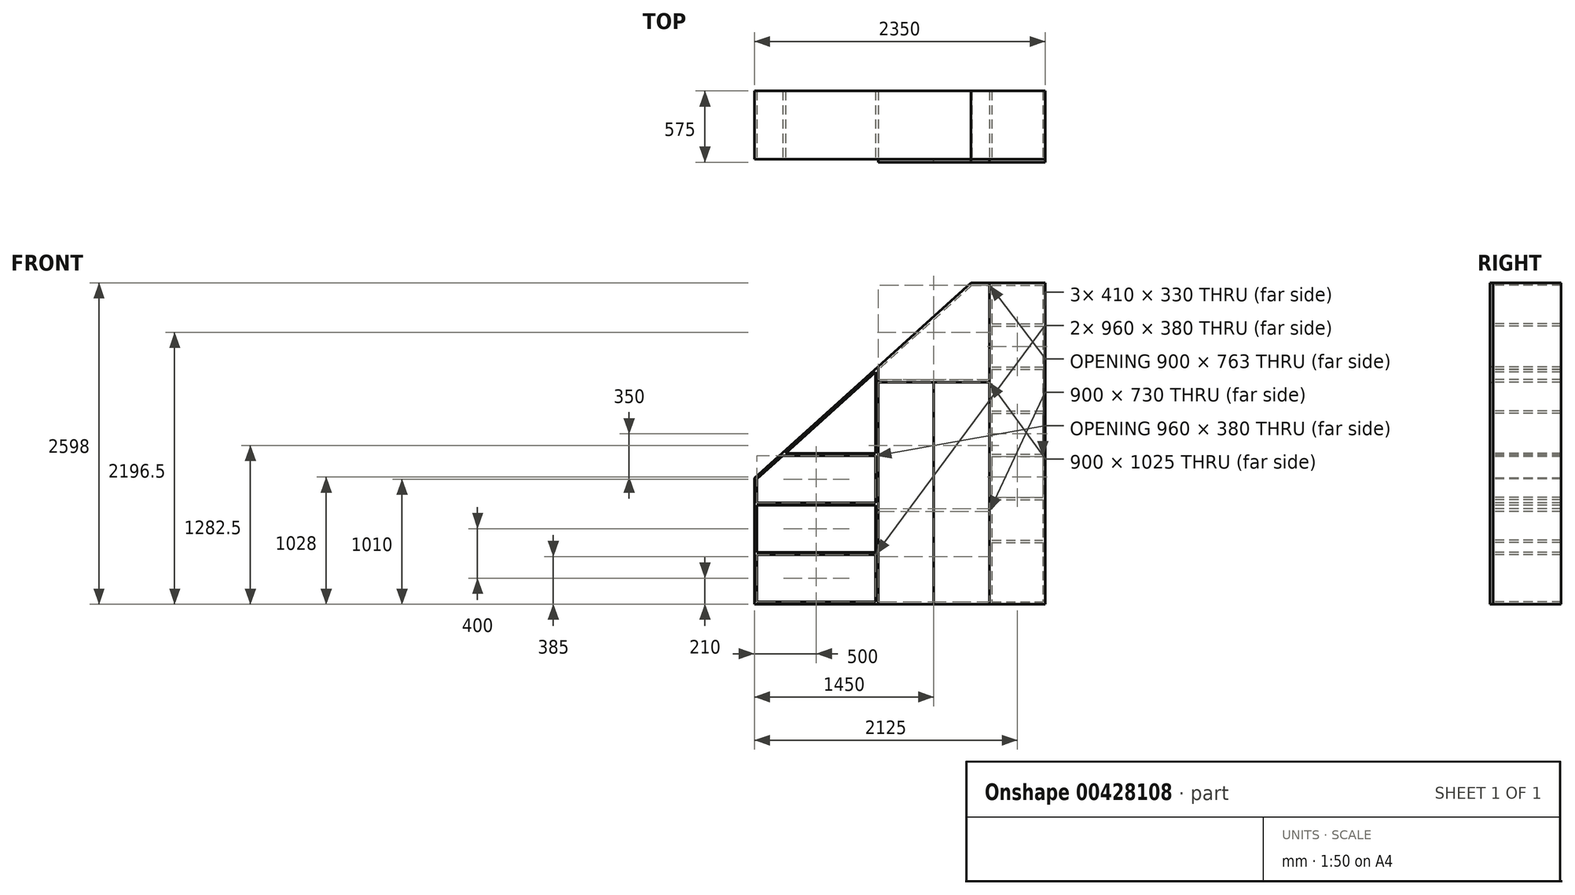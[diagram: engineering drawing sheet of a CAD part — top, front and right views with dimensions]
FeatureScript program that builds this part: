
annotation { "Feature Type Name" : "Feature", "Feature Type Description" : "" }
export const myFeature = defineFeature(function(context is Context, id is Id, definition is map)
    precondition{}
    {
        {
            var Q0;
            Q0=qCreatedBy(makeId("Front.planeOp"),FACE);
            var sketch = newSketch(context, id + "F0", { "sketchPlane" : qUnion([Q0])});
            skLineSegment(sketch, "E0.bottom", {"start": v(500, 1299) * mm, "end": v(1100, 1299) * mm});
            skLineSegment(sketch, "E0.top", {"start": v(-1250, -1299) * mm, "end": v(-250, -1299) * mm});
            skLineSegment(sketch, "E0.right", {"start": v(1100, 1299) * mm, "end": v(1100, -436) * mm});
            skPoint(sketch, "E0.middle", {"position": v(0, 0) * mm});
            skLineSegment(sketch, "E1.0", {"start": v(650, 1279) * mm, "end": v(650, 516) * mm});
            skLineSegment(sketch, "E2.0", {"start": v(200, 1028.49) * mm, "end": v(200, 516) * mm});
            skLineSegment(sketch, "E3.0", {"start": v(-250, 595.78) * mm, "end": v(-250, 516) * mm});
            skLineSegment(sketch, "E4.trimOffspring", {"start": v(650, -1299) * mm, "end": v(1100, -1299) * mm});
            skLineSegment(sketch, "E5", {"start": v(-250, -1299) * mm, "end": v(200, -1299) * mm});
            skLineSegment(sketch, "E6", {"start": v(650, -1299) * mm, "end": v(200, -1299) * mm});
            skLineSegment(sketch, "E7.0", {"start": v(650, -1049) * mm, "end": v(200, -1049) * mm});
            skLineSegment(sketch, "E7.1", {"start": v(-250, -1049) * mm, "end": v(200, -1049) * mm});
            skLineSegment(sketch, "E8.0", {"start": v(650, -799) * mm, "end": v(200, -799) * mm});
            skLineSegment(sketch, "E8.1", {"start": v(-250, -799) * mm, "end": v(200, -799) * mm});
            skLineSegment(sketch, "E9.0", {"start": v(650, -549) * mm, "end": v(200, -549) * mm});
            skLineSegment(sketch, "E9.1", {"start": v(-250, -549) * mm, "end": v(200, -549) * mm});
            skLineSegment(sketch, "E10.0", {"start": v(-250, 516) * mm, "end": v(200, 516) * mm});
            skLineSegment(sketch, "E11", {"start": v(200, 516) * mm, "end": v(650, 516) * mm});
            skLineSegment(sketch, "E12.0", {"start": v(670, 949) * mm, "end": v(1080, 949) * mm});
            skLineSegment(sketch, "E13.0", {"start": v(670, 599) * mm, "end": v(1080, 599) * mm});
            skLineSegment(sketch, "E14.0", {"start": v(670, 264) * mm, "end": v(1080, 264) * mm});
            skLineSegment(sketch, "E15.0", {"start": v(670, -86) * mm, "end": v(1080, -86) * mm});
            skLineSegment(sketch, "E16.0", {"start": v(670, -436) * mm, "end": v(1080, -436) * mm});
            skLineSegment(sketch, "E17.0", {"start": v(670, -801) * mm, "end": v(1080, -801) * mm});
            skLineSegment(sketch, "E18.0", {"start": v(-1230, -899) * mm, "end": v(-270, -899) * mm});
            skLineSegment(sketch, "E19.0", {"start": v(-1230, -499) * mm, "end": v(-270, -499) * mm});
            skLineSegment(sketch, "E20.0", {"start": v(-1020.51, -99) * mm, "end": v(-270, -99) * mm});
            skLineSegment(sketch, "E21.0", {"start": v(-1250, -279) * mm, "end": v(-1250, -1299) * mm});
            skLineSegment(sketch, "E22", {"start": v(500, 1299) * mm, "end": v(-1250, -279) * mm});
            skLineSegment(sketch, "E23", {"start": v(-250, 441.27) * mm, "end": v(650, 441.27) * mm});
            skLineSegment(sketch, "E24.0", {"start": v(-250, 431.27) * mm, "end": v(650, 431.27) * mm});
            skLineSegment(sketch, "E25", {"start": v(200, 516) * mm, "end": v(200, -1279) * mm});
            skLineSegment(sketch, "E26.0", {"start": v(-1230, -287.9) * mm, "end": v(-1230, -479) * mm});
            skLineSegment(sketch, "E27.0", {"start": v(-1230, -1279) * mm, "end": v(-270, -1279) * mm});
            skLineSegment(sketch, "E28.0", {"start": v(-1230, -879) * mm, "end": v(-270, -879) * mm});
            skLineSegment(sketch, "E29.0", {"start": v(-1250, -479) * mm, "end": v(-1247.8, -479) * mm});
            skLineSegment(sketch, "E30.0", {"start": v(507.69, 1279) * mm, "end": v(-250, 595.78) * mm});
            skLineSegment(sketch, "E31.0", {"start": v(507.69, 1279) * mm, "end": v(1080, 1279) * mm});
            skLineSegment(sketch, "E32.0", {"start": v(670, 969) * mm, "end": v(1080, 969) * mm});
            skLineSegment(sketch, "E33.0", {"start": v(670, 619) * mm, "end": v(1080, 619) * mm});
            skLineSegment(sketch, "E34.0", {"start": v(670, 244) * mm, "end": v(1080, 244) * mm});
            skLineSegment(sketch, "E35.0", {"start": v(670, -106) * mm, "end": v(1080, -106) * mm});
            skLineSegment(sketch, "E36.0", {"start": v(670, -456) * mm, "end": v(1080, -456) * mm});
            skLineSegment(sketch, "E37.0", {"start": v(670, -781) * mm, "end": v(1080, -781) * mm});
            skLineSegment(sketch, "E38.0", {"start": v(-250, -1279) * mm, "end": v(200, -1279) * mm});
            skLineSegment(sketch, "E38.1", {"start": v(650, -1279) * mm, "end": v(200, -1279) * mm});
            skLineSegment(sketch, "E39.0", {"start": v(670, -1279) * mm, "end": v(1080, -1279) * mm});
            skLineSegment(sketch, "E40.0", {"start": v(1080, 1279) * mm, "end": v(1080, 969) * mm});
            skLineSegment(sketch, "E41.0", {"start": v(670, 1279) * mm, "end": v(670, 969) * mm});
            skLineSegment(sketch, "E42.0", {"start": v(-270, 577.75) * mm, "end": v(-270, -79) * mm});
            skPoint(sketch, "E43.orphan", {"position": v(-1250, -899) * mm});
            skLineSegment(sketch, "E44.trimOffspring", {"start": v(-1230, -899) * mm, "end": v(-1230, -1279) * mm});
            skLineSegment(sketch, "E45.trimOffspring", {"start": v(-270, -899) * mm, "end": v(-270, -1279) * mm});
            skLineSegment(sketch, "E46.trimOffspring", {"start": v(-250, -899) * mm, "end": v(-250, -1279) * mm});
            skLineSegment(sketch, "E47.trimOffspring", {"start": v(-1230, -479) * mm, "end": v(-270, -479) * mm});
            skLineSegment(sketch, "E48.trimOffspring", {"start": v(-1247.8, -479) * mm, "end": v(-1250, -480.98) * mm});
            skLineSegment(sketch, "E49.trimOffspring", {"start": v(-1230, -499) * mm, "end": v(-1230, -879) * mm});
            skLineSegment(sketch, "E50.trimOffspring", {"start": v(-998.33, -79) * mm, "end": v(-270, -79) * mm});
            skLineSegment(sketch, "E51.trimOffspring", {"start": v(-1020.51, -99) * mm, "end": v(-1230, -287.9) * mm});
            skLineSegment(sketch, "E52.trimOffspring", {"start": v(-270, -99) * mm, "end": v(-270, -479) * mm});
            skLineSegment(sketch, "E53", {"start": v(-250, -879) * mm, "end": v(-250, -899) * mm});
            skPoint(sketch, "E54.orphan", {"position": v(1100, -801) * mm});
            skLineSegment(sketch, "E55.trimOffspring", {"start": v(1080, -801) * mm, "end": v(1080, -1279) * mm});
            skLineSegment(sketch, "E56.trimOffspring", {"start": v(670, -801) * mm, "end": v(670, -1279) * mm});
            skLineSegment(sketch, "E57.trimOffspring", {"start": v(670, -456) * mm, "end": v(670, -781) * mm});
            skLineSegment(sketch, "E58.trimOffspring", {"start": v(1080, -456) * mm, "end": v(1080, -781) * mm});
            skLineSegment(sketch, "E59.trimOffspring", {"start": v(1100, -456) * mm, "end": v(1100, -1299) * mm});
            skLineSegment(sketch, "E60", {"start": v(1100, -436) * mm, "end": v(1100, -456) * mm});
            skLineSegment(sketch, "E61.trimOffspring", {"start": v(1080, -106) * mm, "end": v(1080, -436) * mm});
            skLineSegment(sketch, "E62.trimOffspring", {"start": v(670, -106) * mm, "end": v(670, -436) * mm});
            skLineSegment(sketch, "E63.trimOffspring", {"start": v(670, 244) * mm, "end": v(670, -86) * mm});
            skLineSegment(sketch, "E64.trimOffspring", {"start": v(1080, 244) * mm, "end": v(1080, -86) * mm});
            skLineSegment(sketch, "E65.trimOffspring", {"start": v(1080, 599) * mm, "end": v(1080, 264) * mm});
            skLineSegment(sketch, "E66.trimOffspring", {"start": v(670, 599) * mm, "end": v(670, 264) * mm});
            skLineSegment(sketch, "E67.trimOffspring", {"start": v(670, 949) * mm, "end": v(670, 619) * mm});
            skLineSegment(sketch, "E68.trimOffspring", {"start": v(1080, 949) * mm, "end": v(1080, 619) * mm});
            skLineSegment(sketch, "E69.trimOffspring", {"start": v(-270, 577.75) * mm, "end": v(-998.33, -79) * mm});
            skLineSegment(sketch, "E70.0", {"start": v(650, -529) * mm, "end": v(200, -529) * mm});
            skLineSegment(sketch, "E70.1", {"start": v(-250, -529) * mm, "end": v(200, -529) * mm});
            skLineSegment(sketch, "E71.0", {"start": v(200, 496) * mm, "end": v(650, 496) * mm});
            skLineSegment(sketch, "E71.1", {"start": v(-250, 496) * mm, "end": v(200, 496) * mm});
            skLineSegment(sketch, "E72.trimOffspring", {"start": v(-270, -499) * mm, "end": v(-270, -879) * mm});
            skLineSegment(sketch, "E73.trimOffspring", {"start": v(-250, -549) * mm, "end": v(-250, -879) * mm});
            skLineSegment(sketch, "E74.trimOffspring", {"start": v(650, -549) * mm, "end": v(650, -1279) * mm});
            skLineSegment(sketch, "E75.trimOffspring", {"start": v(-250, 496) * mm, "end": v(-250, -529) * mm});
            skLineSegment(sketch, "E76.trimOffspring", {"start": v(650, 496) * mm, "end": v(650, -529) * mm});
            skLineSegment(sketch, "E77", {"start": v(-270, 577.75) * mm, "end": v(-250, 595.78) * mm});
            skLineSegment(sketch, "E78", {"start": v(-998.33, -79) * mm, "end": v(-1020.51, -99) * mm});
            skLineSegment(sketch, "E79", {"start": v(-250, -529) * mm, "end": v(-250, -549) * mm});
            skLineSegment(sketch, "E80", {"start": v(-250, -1279) * mm, "end": v(-250, -1299) * mm});
            skLineSegment(sketch, "E81", {"start": v(200, -1279) * mm, "end": v(200, -1299) * mm});
            skLineSegment(sketch, "E82", {"start": v(650, -1279) * mm, "end": v(650, -1299) * mm});
            skLineSegment(sketch, "E83", {"start": v(650, -529) * mm, "end": v(650, -549) * mm});
            skLineSegment(sketch, "E84", {"start": v(-1230, -462.94) * mm, "end": v(-1247.8, -479) * mm});
            skLineSegment(sketch, "E85", {"start": v(650, 516) * mm, "end": v(650, 496) * mm});
            skLineSegment(sketch, "E86", {"start": v(650, 1279) * mm, "end": v(650, 1299) * mm});
            skLineSegment(sketch, "E87", {"start": v(-250, 516) * mm, "end": v(-250, 496) * mm});
            skLineSegment(sketch, "E88", {"start": v(-250, 595.78) * mm, "end": v(-250, 622.71) * mm});
            skSolve(sketch);
        }
        {
            var Q0;
            Q0 = qSketchRegion(id + "F0", true);
            var Q1;
            {var subQ1=sQuery(id+"F0.wireOp",EDGE,"E10.0");var subQ3=sQuery(id+"F0.wireOp",EDGE,"bf8423d4-a588-4095-a5d6-ed5b53389bde.0");var subQ4=makeQuery(id+"F0.imprint","INTERSECT",VERTEX,{"derivedFrom":[subQ1,subQ3]});Q1=makeQuery(id+"F0.imprint","IMPRINT",FACE,{"disambiguationData":[TD([[makeQuery(id+"F0.imprint","IMPRINT",EDGE,{"disambiguationData":[TD([[subQ4,-1.0]])],"derivedFrom":subQ3}),1.0]])]});}
            var Q2;
            {var subQ9=sQuery(id+"F0.wireOp",EDGE,"E3.0");Q2=makeQuery(id+"F0.imprint","IMPRINT",FACE,{"disambiguationData":[TD([[makeQuery(id+"F0.imprint","IMPRINT",EDGE,{"derivedFrom":subQ9}),-1.0]])]});}
            var Q3;
            {var subQ0=sQuery(id+"F0.wireOp",EDGE,"E78");Q3=makeQuery(id+"F0.imprint","IMPRINT",FACE,{"disambiguationData":[TD([[makeQuery(id+"F0.imprint","IMPRINT",EDGE,{"derivedFrom":subQ0}),1.0]])]});}
            var Q4;
            {var subQ0=sQuery(id+"F0.wireOp",EDGE,"E31.0");var subQ1=sQuery(id+"F0.wireOp",EDGE,"E1.0");var subQ2=makeQuery(id+"F0.imprint","INTERSECT",VERTEX,{"derivedFrom":[subQ1,subQ0]});Q4=makeQuery(id+"F0.imprint","IMPRINT",FACE,{"disambiguationData":[TD([[makeQuery(id+"F0.imprint","IMPRINT",EDGE,{"disambiguationData":[TD([[subQ2,-1.0]])],"derivedFrom":subQ1}),1.0]])]});}
            var Q5;
            {var subQ0=sQuery(id+"F0.wireOp",EDGE,"E9.1");Q5=makeQuery(id+"F0.imprint","IMPRINT",FACE,{"disambiguationData":[TD([[makeQuery(id+"F0.imprint","IMPRINT",EDGE,{"derivedFrom":subQ0}),1.0]])]});}
            var Q6;
            {var subQ0=sQuery(id+"F0.wireOp",EDGE,"E9.0");Q6=makeQuery(id+"F0.imprint","IMPRINT",FACE,{"disambiguationData":[TD([[makeQuery(id+"F0.imprint","IMPRINT",EDGE,{"derivedFrom":subQ0}),-1.0]])]});}
            var Q7;
            {var subQ0=sQuery(id+"F0.wireOp",EDGE,"E11");Q7=makeQuery(id+"F0.imprint","IMPRINT",FACE,{"disambiguationData":[TD([[makeQuery(id+"F0.imprint","IMPRINT",EDGE,{"derivedFrom":subQ0}),-1.0]])]});}
            var Q8;
            {var subQ0=sQuery(id+"F0.wireOp",EDGE,"E10.0");Q8=makeQuery(id+"F0.imprint","IMPRINT",FACE,{"disambiguationData":[TD([[makeQuery(id+"F0.imprint","IMPRINT",EDGE,{"derivedFrom":subQ0}),-1.0]])]});}
            extrude(context, id + "F1", {"entities" : qUnion([Q0, Q1, Q2, Q3, Q4, Q5, Q6, Q7, Q8]), "oppositeDirection" : true, "depth" : 550 * mm});
        }
        {
            var Q0;
            {var subQ1=sQuery(id+"F0.wireOp",EDGE,"E3.0");Q0=makeQuery(id+"F0.imprint","IMPRINT",FACE,{"disambiguationData":[TD([[makeQuery(id+"F0.imprint","IMPRINT",EDGE,{"derivedFrom":subQ1}),1.0]])]});}
            var Q1;
            {var subQ0=sQuery(id+"F0.wireOp",EDGE,"E10.0");Q1=makeQuery(id+"F0.imprint","IMPRINT",FACE,{"disambiguationData":[TD([[makeQuery(id+"F0.imprint","IMPRINT",EDGE,{"derivedFrom":subQ0}),-1.0]])]});}
            var Q2;
            {var subQ6=sQuery(id+"F0.wireOp",EDGE,"E1.0");Q2=makeQuery(id+"F0.imprint","IMPRINT",FACE,{"disambiguationData":[TD([[makeQuery(id+"F0.imprint","IMPRINT",EDGE,{"derivedFrom":subQ6}),-1.0]])]});}
            var Q3;
            {var subQ0=sQuery(id+"F0.wireOp",EDGE,"E11");Q3=makeQuery(id+"F0.imprint","IMPRINT",FACE,{"disambiguationData":[TD([[makeQuery(id+"F0.imprint","IMPRINT",EDGE,{"derivedFrom":subQ0}),-1.0]])]});}
            var Q4;
            {var subQ5=sQuery(id+"F0.wireOp",EDGE,"E88");Q4=makeQuery(id+"F0.imprint","IMPRINT",FACE,{"disambiguationData":[TD([[makeQuery(id+"F0.imprint","IMPRINT",EDGE,{"derivedFrom":subQ5}),-1.0]])]});}
            var Q5;
            {var subQ9=sQuery(id+"F0.wireOp",EDGE,"E86");Q5=makeQuery(id+"F0.imprint","IMPRINT",FACE,{"disambiguationData":[TD([[makeQuery(id+"F0.imprint","IMPRINT",EDGE,{"derivedFrom":subQ9}),1.0]])]});}
            extrude(context, id + "F2", {"entities" : qUnion([Q0, Q1, Q2, Q3, Q4, Q5]), "depth" : 25 * mm});
        }
        {
            var Q0;
            {var subQ5=sQuery(id+"F0.wireOp",EDGE,"E71.1");Q0=makeQuery(id+"F0.imprint","IMPRINT",FACE,{"disambiguationData":[TD([[makeQuery(id+"F0.imprint","IMPRINT",EDGE,{"derivedFrom":subQ5}),-1.0]])]});}
            var Q1;
            {var subQ5=sQuery(id+"F0.wireOp",EDGE,"E70.1");Q1=makeQuery(id+"F0.imprint","IMPRINT",FACE,{"disambiguationData":[TD([[makeQuery(id+"F0.imprint","IMPRINT",EDGE,{"derivedFrom":subQ5}),1.0]])]});}
            var Q2;
            {var subQ0=sQuery(id+"F0.wireOp",EDGE,"E75.trimOffspring");var subQ1=sQuery(id+"F0.wireOp",EDGE,"E23");var subQ2=makeQuery(id+"F0.imprint","INTERSECT",VERTEX,{"derivedFrom":[subQ1,subQ0]});Q2=makeQuery(id+"F0.imprint","IMPRINT",FACE,{"disambiguationData":[TD([[makeQuery(id+"F0.imprint","IMPRINT",EDGE,{"disambiguationData":[TD([[subQ2,-1.0]])],"derivedFrom":subQ1}),-1.0]])]});}
            var Q3;
            {var subQ0=sQuery(id+"F0.wireOp",EDGE,"E8.1");Q3=makeQuery(id+"F0.imprint","IMPRINT",FACE,{"disambiguationData":[TD([[makeQuery(id+"F0.imprint","IMPRINT",EDGE,{"derivedFrom":subQ0}),1.0]])]});}
            var Q4;
            {var subQ1=sQuery(id+"F0.wireOp",EDGE,"E7.1");Q4=makeQuery(id+"F0.imprint","IMPRINT",FACE,{"disambiguationData":[TD([[makeQuery(id+"F0.imprint","IMPRINT",EDGE,{"derivedFrom":subQ1}),1.0]])]});}
            var Q5;
            {var subQ0=sQuery(id+"F0.wireOp",EDGE,"E7.1");Q5=makeQuery(id+"F0.imprint","IMPRINT",FACE,{"disambiguationData":[TD([[makeQuery(id+"F0.imprint","IMPRINT",EDGE,{"derivedFrom":subQ0}),-1.0]])]});}
            var Q6;
            {var subQ0=sQuery(id+"F0.wireOp",EDGE,"E9.1");Q6=makeQuery(id+"F0.imprint","IMPRINT",FACE,{"disambiguationData":[TD([[makeQuery(id+"F0.imprint","IMPRINT",EDGE,{"derivedFrom":subQ0}),1.0]])]});}
            var Q7;
            Q7=makeQuery(id+"F0.imprint","IMPRINT",FACE,{"disambiguationData":[TD([[makeQuery(id+"F0.imprint","IMPRINT",EDGE,{"derivedFrom":sQuery(id+"F0.wireOp",EDGE,"E5")}),1.0]])]});
            extrude(context, id + "F3", {"entities" : qUnion([Q0, Q1, Q2, Q3, Q4, Q5, Q6, Q7]), "depth" : 25 * mm});
        }
        {
            var Q0;
            {var subQ0=sQuery(id+"F0.wireOp",EDGE,"E7.0");Q0=makeQuery(id+"F0.imprint","IMPRINT",FACE,{"disambiguationData":[TD([[makeQuery(id+"F0.imprint","IMPRINT",EDGE,{"derivedFrom":subQ0}),1.0]])]});}
            var Q1;
            {var subQ0=sQuery(id+"F0.wireOp",EDGE,"E7.0");Q1=makeQuery(id+"F0.imprint","IMPRINT",FACE,{"disambiguationData":[TD([[makeQuery(id+"F0.imprint","IMPRINT",EDGE,{"derivedFrom":subQ0}),-1.0]])]});}
            var Q2;
            Q2=makeQuery(id+"F0.imprint","IMPRINT",FACE,{"disambiguationData":[TD([[makeQuery(id+"F0.imprint","IMPRINT",EDGE,{"derivedFrom":sQuery(id+"F0.wireOp",EDGE,"E6")}),-1.0]])]});
            var Q3;
            {var subQ0=sQuery(id+"F0.wireOp",EDGE,"E8.0");Q3=makeQuery(id+"F0.imprint","IMPRINT",FACE,{"disambiguationData":[TD([[makeQuery(id+"F0.imprint","IMPRINT",EDGE,{"derivedFrom":subQ0}),-1.0]])]});}
            var Q4;
            {var subQ0=sQuery(id+"F0.wireOp",EDGE,"E9.0");Q4=makeQuery(id+"F0.imprint","IMPRINT",FACE,{"disambiguationData":[TD([[makeQuery(id+"F0.imprint","IMPRINT",EDGE,{"derivedFrom":subQ0}),-1.0]])]});}
            var Q5;
            {var subQ5=sQuery(id+"F0.wireOp",EDGE,"E70.0");Q5=makeQuery(id+"F0.imprint","IMPRINT",FACE,{"disambiguationData":[TD([[makeQuery(id+"F0.imprint","IMPRINT",EDGE,{"derivedFrom":subQ5}),-1.0]])]});}
            var Q6;
            {var subQ5=sQuery(id+"F0.wireOp",EDGE,"E71.0");Q6=makeQuery(id+"F0.imprint","IMPRINT",FACE,{"disambiguationData":[TD([[makeQuery(id+"F0.imprint","IMPRINT",EDGE,{"derivedFrom":subQ5}),-1.0]])]});}
            var Q7;
            {var subQ0=sQuery(id+"F0.wireOp",EDGE,"E76.trimOffspring");var subQ1=sQuery(id+"F0.wireOp",EDGE,"E23");var subQ2=makeQuery(id+"F0.imprint","INTERSECT",VERTEX,{"derivedFrom":[subQ1,subQ0]});Q7=makeQuery(id+"F0.imprint","IMPRINT",FACE,{"disambiguationData":[TD([[makeQuery(id+"F0.imprint","IMPRINT",EDGE,{"disambiguationData":[TD([[subQ2,1.0]])],"derivedFrom":subQ1}),-1.0]])]});}
            extrude(context, id + "F4", {"entities" : qUnion([Q0, Q1, Q2, Q3, Q4, Q5, Q6, Q7]), "depth" : 25 * mm});
        }
        {
            var Q0;
            {var subQ18=sQuery(id+"F0.wireOp",EDGE,"E0.right");Q0=makeQuery(id+"F0.imprint","IMPRINT",FACE,{"disambiguationData":[TD([[makeQuery(id+"F0.imprint","IMPRINT",EDGE,{"derivedFrom":subQ18}),-1.0]])]});}
            var Q1;
            {var subQ0=sQuery(id+"F0.wireOp",EDGE,"E32.0");Q1=makeQuery(id+"F0.imprint","IMPRINT",FACE,{"disambiguationData":[TD([[makeQuery(id+"F0.imprint","IMPRINT",EDGE,{"derivedFrom":subQ0}),1.0]])]});}
            var Q2;
            Q2=makeQuery(id+"F0.imprint","IMPRINT",FACE,{"disambiguationData":[TD([[makeQuery(id+"F0.imprint","IMPRINT",EDGE,{"derivedFrom":sQuery(id+"F0.wireOp",EDGE,"E12.0")}),-1.0]])]});
            var Q3;
            Q3=makeQuery(id+"F0.imprint","IMPRINT",FACE,{"disambiguationData":[TD([[makeQuery(id+"F0.imprint","IMPRINT",EDGE,{"derivedFrom":sQuery(id+"F0.wireOp",EDGE,"E13.0")}),-1.0]])]});
            var Q4;
            Q4=makeQuery(id+"F0.imprint","IMPRINT",FACE,{"disambiguationData":[TD([[makeQuery(id+"F0.imprint","IMPRINT",EDGE,{"derivedFrom":sQuery(id+"F0.wireOp",EDGE,"E15.0")}),1.0]])]});
            var Q5;
            Q5=makeQuery(id+"F0.imprint","IMPRINT",FACE,{"disambiguationData":[TD([[makeQuery(id+"F0.imprint","IMPRINT",EDGE,{"derivedFrom":sQuery(id+"F0.wireOp",EDGE,"E16.0")}),1.0]])]});
            var Q6;
            Q6=makeQuery(id+"F0.imprint","IMPRINT",FACE,{"disambiguationData":[TD([[makeQuery(id+"F0.imprint","IMPRINT",EDGE,{"derivedFrom":sQuery(id+"F0.wireOp",EDGE,"E36.0")}),-1.0]])]});
            var Q7;
            Q7=makeQuery(id+"F0.imprint","IMPRINT",FACE,{"disambiguationData":[TD([[makeQuery(id+"F0.imprint","IMPRINT",EDGE,{"derivedFrom":sQuery(id+"F0.wireOp",EDGE,"E17.0")}),-1.0]])]});
            var Q8;
            {var subQ0=sQuery(id+"F0.wireOp",EDGE,"E31.0");var subQ1=sQuery(id+"F0.wireOp",EDGE,"bf8423d4-a588-4095-a5d6-ed5b53389bde.0");var subQ2=makeQuery(id+"F0.imprint","INTERSECT",VERTEX,{"derivedFrom":[subQ1,subQ0]});Q8=makeQuery(id+"F0.imprint","IMPRINT",FACE,{"disambiguationData":[TD([[makeQuery(id+"F0.imprint","IMPRINT",EDGE,{"disambiguationData":[TD([[subQ2,-1.0]])],"derivedFrom":subQ1}),-1.0]])]});}
            var Q9;
            {var subQ1=sQuery(id+"F0.wireOp",EDGE,"E1.0");var subQ3=sQuery(id+"F0.wireOp",EDGE,"bf8423d4-a588-4095-a5d6-ed5b53389bde.0");var subQ4=makeQuery(id+"F0.imprint","INTERSECT",VERTEX,{"derivedFrom":[subQ1,subQ3]});Q9=makeQuery(id+"F0.imprint","IMPRINT",FACE,{"disambiguationData":[TD([[makeQuery(id+"F0.imprint","IMPRINT",EDGE,{"disambiguationData":[TD([[subQ4,1.0]])],"derivedFrom":subQ3}),-1.0]])]});}
            var Q10;
            {var subQ6=sQuery(id+"F0.wireOp",EDGE,"E86");Q10=makeQuery(id+"F0.imprint","IMPRINT",FACE,{"disambiguationData":[TD([[makeQuery(id+"F0.imprint","IMPRINT",EDGE,{"derivedFrom":subQ6}),-1.0]])]});}
            extrude(context, id + "F5", {"entities" : qUnion([Q0, Q1, Q2, Q3, Q4, Q5, Q6, Q7, Q8, Q9, Q10]), "depth" : 25 * mm});
        }
    });
